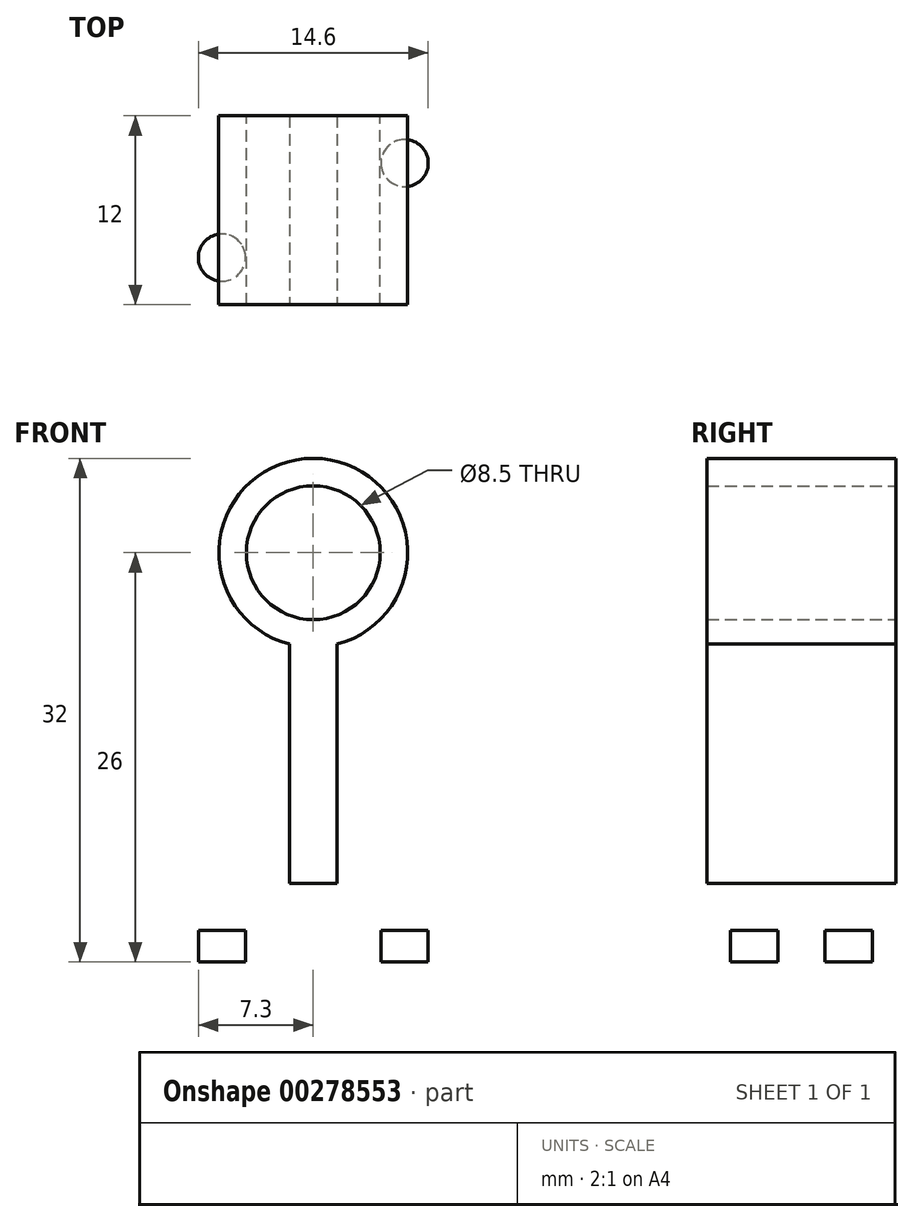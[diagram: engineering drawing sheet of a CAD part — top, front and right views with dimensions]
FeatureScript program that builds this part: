
annotation { "Feature Type Name" : "Feature", "Feature Type Description" : "" }
export const myFeature = defineFeature(function(context is Context, id is Id, definition is map)
    precondition{}
    {
        {
            var Q0;
            Q0=qCreatedBy(makeId("Front.planeOp"),FACE);
            var sketch = newSketch(context, id + "F0", { "sketchPlane" : qUnion([Q0])});
            skCircle(sketch, "E0", {"center": v(0, 25) * mm, "radius": 4.25 * mm});
            skCircle(sketch, "E1", {"center": v(0, 25) * mm, "radius": 6 * mm});
            skLineSegment(sketch, "E2.bottom", {"start": v(-1.5, 0) * mm, "end": v(1.5, 0) * mm});
            skLineSegment(sketch, "E2.top", {"start": v(-1.5, 25) * mm, "end": v(1.5, 25) * mm});
            skLineSegment(sketch, "E2.left", {"start": v(-1.5, 0) * mm, "end": v(-1.5, 25) * mm});
            skLineSegment(sketch, "E2.right", {"start": v(1.5, 0) * mm, "end": v(1.5, 25) * mm});
            skLineSegment(sketch, "E3.bottom", {"start": v(7.5, 1) * mm, "end": v(-7.5, 1) * mm});
            skLineSegment(sketch, "E3.top", {"start": v(7.5, -1) * mm, "end": v(-7.5, -1) * mm});
            skLineSegment(sketch, "E3.left", {"start": v(7.5, 1) * mm, "end": v(7.5, -1) * mm});
            skLineSegment(sketch, "E3.right", {"start": v(-7.5, 1) * mm, "end": v(-7.5, -1) * mm});
            skPoint(sketch, "E3.middle", {"position": v(0, 0) * mm});
            skSolve(sketch);
        }
        {
            var Q0;
            {var subQ0=sQuery(id+"F0.wireOp",EDGE,"E2.left");var subQ1=sQuery(id+"F0.wireOp",EDGE,"E0");var subQ2=makeQuery(id+"F0.imprint","INTERSECT",VERTEX,{"derivedFrom":[subQ1,subQ0]});Q0=makeQuery(id+"F0.imprint","IMPRINT",FACE,{"disambiguationData":[TD([[makeQuery(id+"F0.imprint","IMPRINT",EDGE,{"disambiguationData":[TD([[subQ2,1.0]])],"derivedFrom":subQ1}),-1.0]])]});}
            var Q1;
            {var subQ0=sQuery(id+"F0.wireOp",EDGE,"E2.left");var subQ1=sQuery(id+"F0.wireOp",EDGE,"E0");var subQ2=makeQuery(id+"F0.imprint","INTERSECT",VERTEX,{"derivedFrom":[subQ1,subQ0]});Q1=makeQuery(id+"F0.imprint","IMPRINT",FACE,{"disambiguationData":[TD([[makeQuery(id+"F0.imprint","IMPRINT",EDGE,{"disambiguationData":[TD([[subQ2,-1.0]])],"derivedFrom":subQ1}),-1.0]])]});}
            var Q2;
            {var subQ0=sQuery(id+"F0.wireOp",EDGE,"E2.left");var subQ1=sQuery(id+"F0.wireOp",EDGE,"E1");var subQ2=makeQuery(id+"F0.imprint","INTERSECT",VERTEX,{"derivedFrom":[subQ1,subQ0]});Q2=makeQuery(id+"F0.imprint","IMPRINT",FACE,{"disambiguationData":[TD([[makeQuery(id+"F0.imprint","IMPRINT",EDGE,{"disambiguationData":[TD([[subQ2,-1.0]])],"derivedFrom":subQ1}),-1.0]])]});}
            var Q3;
            {var subQ1=sQuery(id+"F0.wireOp",EDGE,"E2.bottom");Q3=makeQuery(id+"F0.imprint","IMPRINT",FACE,{"disambiguationData":[TD([[makeQuery(id+"F0.imprint","IMPRINT",EDGE,{"derivedFrom":subQ1}),-1.0]])]});}
            var Q4;
            {var subQ0=sQuery(id+"F0.wireOp",EDGE,"E2.bottom");Q4=makeQuery(id+"F0.imprint","IMPRINT",FACE,{"disambiguationData":[TD([[makeQuery(id+"F0.imprint","IMPRINT",EDGE,{"derivedFrom":subQ0}),1.0]])]});}
            extrude(context, id + "F1", {"entities" : qUnion([Q0, Q1, Q2, Q3, Q4]), "depth" : 12 * mm});
        }
        {
            var Q0;
            Q0=makeQuery(id+"F1.opExtrude","SWEPT_FACE",FACE,{"disambiguationData":[OSD([sQuery(id+"F0.wireOp",EDGE,"E3.top")])]});
            var sketch = newSketch(context, id + "F2", { "sketchPlane" : qUnion([Q0])});
            skCircle(sketch, "E4", {"center": v(-5.8, 3) * mm, "radius": 1.5 * mm});
            skLineSegment(sketch, "E5", {"start": v(-7.5, 6) * mm, "end": v(7.5, 6) * mm, "construction": true});
            skLineSegment(sketch, "E6", {"start": v(0, 12) * mm, "end": v(0, 0) * mm, "construction": true});
            skCircle(sketch, "E7.MirrorC", {"center": v(-5.8, 9) * mm, "radius": 1.5 * mm});
            skCircle(sketch, "E8.MirrorC", {"center": v(5.8, 9) * mm, "radius": 1.5 * mm});
            skCircle(sketch, "E9.MirrorC", {"center": v(5.8, 3) * mm, "radius": 1.5 * mm});
            skSolve(sketch);
        }
        {
            var Q0;
            Q0=makeQuery(id+"F2.imprint","IMPRINT",FACE,{"disambiguationData":[TD([[makeQuery(id+"F2.imprint","IMPRINT",EDGE,{"derivedFrom":sQuery(id+"F2.wireOp",EDGE,"E7.MirrorC")}),-1.0]])]});
            var Q1;
            Q1=makeQuery(id+"F2.imprint","IMPRINT",FACE,{"disambiguationData":[TD([[makeQuery(id+"F2.imprint","IMPRINT",EDGE,{"derivedFrom":sQuery(id+"F2.wireOp",EDGE,"E4")}),1.0]])]});
            var Q2;
            Q2=makeQuery(id+"F2.imprint","IMPRINT",FACE,{"disambiguationData":[TD([[makeQuery(id+"F2.imprint","IMPRINT",EDGE,{"derivedFrom":sQuery(id+"F2.wireOp",EDGE,"E9.MirrorC")}),-1.0]])]});
            var Q3;
            Q3=makeQuery(id+"F2.imprint","IMPRINT",FACE,{"disambiguationData":[TD([[makeQuery(id+"F2.imprint","IMPRINT",EDGE,{"derivedFrom":sQuery(id+"F2.wireOp",EDGE,"E8.MirrorC")}),1.0]])]});
            var Q4;
            {var subQ0=sQuery(id+"F0.wireOp",EDGE,"E3.bottom");Q4=makeQuery(id+"F1.opExtrude","SWEPT_FACE",FACE,{"disambiguationData":[OSD([subQ0]),TDD([makeQuery(id+"F0.imprint","IMPRINT",EDGE,{"disambiguationData":[TD([[makeQuery(id+"F0.imprint","INTERSECT",VERTEX,{"derivedFrom":[subQ0,sQuery(id+"F0.wireOp",EDGE,"E3.left")]}),-1.0]])],"derivedFrom":subQ0})])]});}
            extrude(context, id + "F3", {"entities" : qUnion([Q0, Q1, Q2, Q3]), "operationType" : NewBodyOperationType.REMOVE, "oppositeDirection" : true, "endBoundEntityFace" : qUnion([Q4]), "depth" : 5 * mm});
        }
    });
